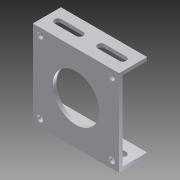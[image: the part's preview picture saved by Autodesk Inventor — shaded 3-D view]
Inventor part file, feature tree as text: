
AUTODESK INVENTOR PART (.ipt)
format: ipt  version: 2012 (Build 160160000, 160)  size: 158,208 bytes
history: native  units: in
note: dims shown in document units (in); Inventor stores cm internally (conversion verified against a paired STEP export)
features: sketch x3, extrude x3, hole x1, fillet x1
ambient origin geometry x8: Origin, YZ Plane, XZ Plane, XY Plane, X Axis, Y Axis, Z Axis, Center Point
bodies: Solid1 (feature_tree)
feature tree (8):
  sketch  "Sketch1"  dims[d0=3.0in d1=3.0in]
  extrude  "Extrusion1"  Depth=3.0in
  hole  "Hole1"  [1 undecoded]
  extrude  "Extrusion2"  Depth=0.25in
  extrude  "Extrusion3"  Depth=0.25in
  fillet  "Fillet1"  Radius=0.25in
  sketch  "Sketch3"  dims[d2=1.5in d3=1.5in]
  sketch  "Sketch4"  dims[d4=1.615in d5=0.25in d6=0.25in d7=0.25in d8=0.25in d10=0.125in d11=0.0in d12=0.2in d13=0.75in d14=0.375in d15=0.25in d16=0.5635in d17=1.0in d18=0.8108in d32=0.125in d33=0.125in d34=0.85in d35=0.0in d36=0.25in d37=0.375in d38=0.25in d39=0.25in d40=1.0in d41=0.25in d42=1.0in d43=1.0in d44=0.0in d45=0.125in]
note: 1 required parameter value undecoded (feature->parameter linkage not recoverable at this tier; creation-order binding heuristic only, values carry confidence <= 0.55)
